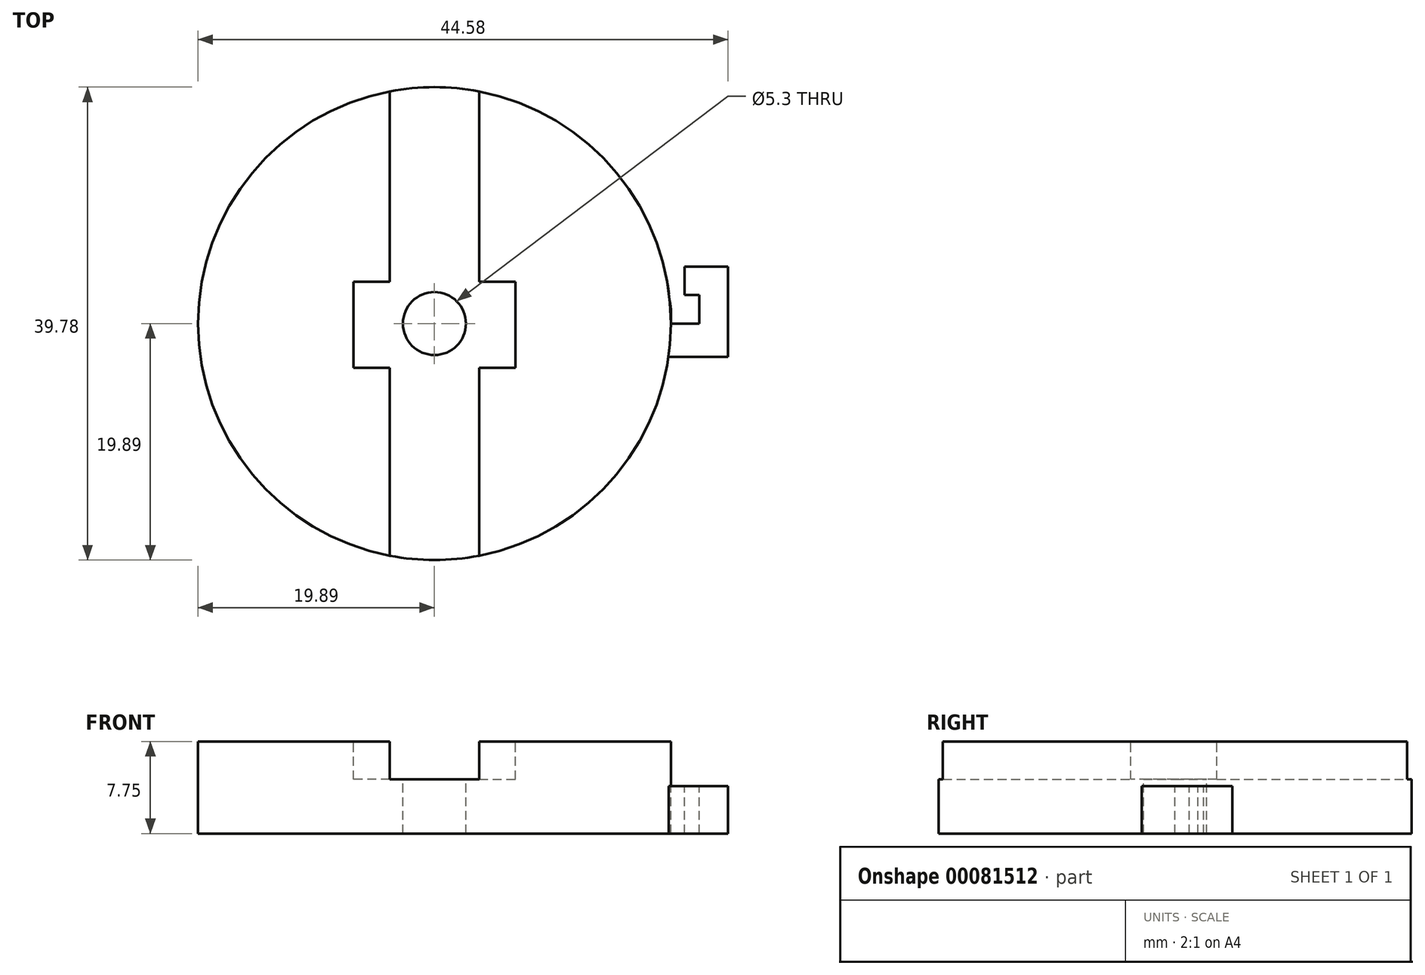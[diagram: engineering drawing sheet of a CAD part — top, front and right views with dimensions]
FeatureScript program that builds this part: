
annotation { "Feature Type Name" : "Feature", "Feature Type Description" : "" }
export const myFeature = defineFeature(function(context is Context, id is Id, definition is map)
    precondition{}
    {
        {
            var Q0;
            Q0=qCreatedBy(makeId("Top.planeOp"),FACE);
            var sketch = newSketch(context, id + "F0", { "sketchPlane" : qUnion([Q0])});
            skCircle(sketch, "E0", {"center": v(0, 0) * mm, "radius": 19.89 * mm});
            skSolve(sketch);
        }
        {
            var Q0;
            Q0 = qSketchRegion(id + "F0", true);
            extrude(context, id + "F1", {"entities" : qUnion([Q0]), "depth" : 7.75 * mm});
        }
        {
            var Q0;
            Q0=makeQuery(id+"F1.opExtrude","CAP_FACE",FACE,{"disambiguationData":[OSD([sQuery(id+"F0.wireOp",EDGE,"E0")])],"isStart":false});
            var sketch = newSketch(context, id + "F2", { "sketchPlane" : qUnion([Q0])});
            skLineSegment(sketch, "E1.bottom", {"start": v(3.75, -20.85) * mm, "end": v(-3.75, -20.85) * mm});
            skLineSegment(sketch, "E1.top", {"start": v(3.75, 20.85) * mm, "end": v(-3.75, 20.85) * mm});
            skLineSegment(sketch, "E1.left", {"start": v(3.75, -20.85) * mm, "end": v(3.75, 20.85) * mm});
            skLineSegment(sketch, "E1.right", {"start": v(-3.75, -20.85) * mm, "end": v(-3.75, 20.85) * mm});
            skPoint(sketch, "E1.middle", {"position": v(0, 0) * mm});
            skLineSegment(sketch, "E2.bottom", {"start": v(3.75, 3.51) * mm, "end": v(6.81, 3.51) * mm});
            skLineSegment(sketch, "E2.top", {"start": v(3.75, -3.74) * mm, "end": v(6.81, -3.74) * mm});
            skLineSegment(sketch, "E2.left", {"start": v(3.75, 3.51) * mm, "end": v(3.75, -3.74) * mm});
            skLineSegment(sketch, "E2.right", {"start": v(6.81, 3.51) * mm, "end": v(6.81, -3.74) * mm});
            skLineSegment(sketch, "E3.bottom", {"start": v(-3.75, 3.51) * mm, "end": v(-6.81, 3.51) * mm});
            skLineSegment(sketch, "E3.top", {"start": v(-3.75, -3.74) * mm, "end": v(-6.8, -3.74) * mm});
            skLineSegment(sketch, "E3.left", {"start": v(-3.75, 3.51) * mm, "end": v(-3.75, -3.74) * mm});
            skLineSegment(sketch, "E3.right", {"start": v(-6.81, 3.51) * mm, "end": v(-6.8, -3.74) * mm});
            skSolve(sketch);
        }
        {
            var Q0;
            Q0 = qSketchRegion(id + "F2", true);
            extrude(context, id + "F3", {"entities" : qUnion([Q0]), "operationType" : NewBodyOperationType.REMOVE, "oppositeDirection" : true, "depth" : 3.2 * mm});
        }
        {
            var Q0;
            Q0=qCreatedBy(makeId("Right.planeOp"),FACE);
            var sketch = newSketch(context, id + "F4", { "sketchPlane" : qUnion([Q0])});
            skLineSegment(sketch, "E4.bottom", {"start": v(-2.8, 4) * mm, "end": v(0, 4) * mm});
            skLineSegment(sketch, "E4.top", {"start": v(-2.8, 0) * mm, "end": v(0, 0) * mm});
            skLineSegment(sketch, "E4.left", {"start": v(-2.8, 4) * mm, "end": v(-2.8, 0) * mm});
            skLineSegment(sketch, "E4.right", {"start": v(0, 4) * mm, "end": v(0, 0) * mm});
            skLineSegment(sketch, "E5.bottom", {"start": v(-2.8, 4) * mm, "end": v(5.4, 4) * mm});
            skLineSegment(sketch, "E5.top", {"start": v(-2.8, 0) * mm, "end": v(5.4, 0) * mm});
            skLineSegment(sketch, "E5.right", {"start": v(5.4, 4) * mm, "end": v(5.4, 0) * mm});
            skSolve(sketch);
        }
        {
            var Q0;
            Q0 = qSketchRegion(id + "F4", true);
            extrude(context, id + "F5", {"entities" : qUnion([Q0]), "operationType" : NewBodyOperationType.ADD, "depth" : 25.21 * mm});
        }
        {
            var Q0;
            Q0=makeQuery(id+"F5.opExtrude","SWEPT_FACE",FACE,{"disambiguationData":[OSD([sQuery(id+"F4.wireOp",EDGE,"E5.bottom")])]});
            var sketch = newSketch(context, id + "F6", { "sketchPlane" : qUnion([Q0])});
            skLineSegment(sketch, "E6.bottom", {"start": v(19.89, 0) * mm, "end": v(22.29, 0) * mm});
            skLineSegment(sketch, "E6.top", {"start": v(19.89, 2.4) * mm, "end": v(22.29, 2.4) * mm});
            skLineSegment(sketch, "E6.left", {"start": v(19.89, 0) * mm, "end": v(19.89, 2.4) * mm});
            skLineSegment(sketch, "E6.right", {"start": v(22.29, 0) * mm, "end": v(22.29, 2.4) * mm});
            skSolve(sketch);
        }
        {
            var Q0;
            Q0 = qSketchRegion(id + "F6", true);
            extrude(context, id + "F7", {"entities" : qUnion([Q0]), "operationType" : NewBodyOperationType.REMOVE, "oppositeDirection" : true, "depth" : 4 * mm});
        }
        {
            var Q0;
            Q0=makeQuery(id+"F5.opExtrude","SWEPT_FACE",FACE,{"disambiguationData":[OSD([sQuery(id+"F4.wireOp",EDGE,"E5.bottom")])]});
            var sketch = newSketch(context, id + "F8", { "sketchPlane" : qUnion([Q0])});
            skLineSegment(sketch, "E7", {"start": v(19.89, 0) * mm, "end": v(19.89, 5.4) * mm});
            skLineSegment(sketch, "E8", {"start": v(19.89, 5.4) * mm, "end": v(19.14, 5.4) * mm});
            skFitSpline(sketch, "E9", {"points": [v(19.14, 5.4) * mm, v(19.3, 4.79) * mm, v(19.44, 4.17) * mm, v(19.6, 3.4) * mm, v(19.72, 2.52) * mm, v(19.8, 1.92) * mm, v(19.89, 1.2) * mm, v(19.89, 0.38) * mm, v(19.89, 0) * mm], "startDerivative": vector(1.2, -5.13) * mm, "endDerivative": vector(0.05, -3.6) * mm});
            skSolve(sketch);
        }
        {
            var Q0;
            {var subQ11=sQuery(id+"F8.wireOp",EDGE,"E8");Q0=makeQuery(id+"F8.imprint","IMPRINT",FACE,{"disambiguationData":[TD([[makeQuery(id+"F8.imprint","IMPRINT",EDGE,{"derivedFrom":subQ11}),1.0]])]});}
            extrude(context, id + "F9", {"entities" : qUnion([Q0]), "operationType" : NewBodyOperationType.REMOVE, "endBound" : BoundingType.THROUGH_ALL, "oppositeDirection" : true, "depth" : 25 * mm});
        }
        {
            var Q0;
            {var subQ3=sQuery(id+"F4.wireOp",EDGE,"E5.bottom");var subQ4=makeQuery(id+"F5.opExtrude","SWEPT_FACE",FACE,{"disambiguationData":[OSD([subQ3])]});var subQ6=sQuery(id+"F4.wireOp",EDGE,"E4.left");Q0=makeQuery(id+"F9.boolean.opBoolean","SPLIT",FACE,{"disambiguationData":[TD([makeQuery(id+"F5.opExtrude","SWEPT_FACE",FACE,{"disambiguationData":[OSD([subQ6])]})])],"derivedFrom":subQ4});}
            var sketch = newSketch(context, id + "F10", { "sketchPlane" : qUnion([Q0])});
            skLineSegment(sketch, "E10", {"start": v(19.74, 2.4) * mm, "end": v(21.04, 2.4) * mm});
            skLineSegment(sketch, "E11", {"start": v(21.04, 2.4) * mm, "end": v(21.04, 5.4) * mm});
            skLineSegment(sketch, "E12", {"start": v(21.04, 5.4) * mm, "end": v(19.89, 5.4) * mm});
            skLineSegment(sketch, "E13", {"start": v(19.89, 5.4) * mm, "end": v(19.74, 2.4) * mm});
            skSolve(sketch);
        }
        {
            var Q0;
            Q0 = qSketchRegion(id + "F10", true);
            extrude(context, id + "F11", {"entities" : qUnion([Q0]), "operationType" : NewBodyOperationType.REMOVE, "endBound" : BoundingType.THROUGH_ALL, "oppositeDirection" : true, "depth" : 25 * mm});
        }
        {
            var Q0;
            {var subQ3=sQuery(id+"F4.wireOp",EDGE,"E5.bottom");var subQ4=makeQuery(id+"F5.opExtrude","SWEPT_FACE",FACE,{"disambiguationData":[OSD([subQ3])]});var subQ6=sQuery(id+"F4.wireOp",EDGE,"E4.left");Q0=makeQuery(id+"F9.boolean.opBoolean","SPLIT",FACE,{"disambiguationData":[TD([makeQuery(id+"F5.opExtrude","SWEPT_FACE",FACE,{"disambiguationData":[OSD([subQ6])]})])],"derivedFrom":subQ4});}
            var sketch = newSketch(context, id + "F12", { "sketchPlane" : qUnion([Q0])});
            skLineSegment(sketch, "E14.bottom", {"start": v(25.21, 5.4) * mm, "end": v(24.69, 5.4) * mm});
            skLineSegment(sketch, "E14.top", {"start": v(25.21, -2.8) * mm, "end": v(24.69, -2.8) * mm});
            skLineSegment(sketch, "E14.left", {"start": v(25.21, 5.4) * mm, "end": v(25.21, -2.8) * mm});
            skLineSegment(sketch, "E14.right", {"start": v(24.69, 4.8) * mm, "end": v(24.69, -2.8) * mm});
            skLineSegment(sketch, "E15.bottom", {"start": v(21.04, 5.4) * mm, "end": v(25.21, 5.4) * mm});
            skLineSegment(sketch, "E15.top", {"start": v(21.04, 4.8) * mm, "end": v(24.69, 4.8) * mm});
            skLineSegment(sketch, "E15.left", {"start": v(21.04, 5.4) * mm, "end": v(21.04, 4.8) * mm});
            skLineSegment(sketch, "E15.right", {"start": v(25.21, 5.4) * mm, "end": v(25.21, 4.8) * mm});
            skSolve(sketch);
        }
        {
            var Q0;
            Q0 = qSketchRegion(id + "F12", true);
            extrude(context, id + "F13", {"entities" : qUnion([Q0]), "operationType" : NewBodyOperationType.REMOVE, "endBound" : BoundingType.THROUGH_ALL, "oppositeDirection" : true, "depth" : 25 * mm});
        }
        {
            var Q0;
            Q0=makeQuery(id+"F3.boolean.opBoolean","COPY",FACE,{"derivedFrom":makeQuery(id+"F3.opExtrude","CAP_FACE",FACE,{"disambiguationData":[OSD([sQuery(id+"F2.wireOp",EDGE,"E1.bottom"),sQuery(id+"F2.wireOp",EDGE,"E1.top"),sQuery(id+"F2.wireOp",EDGE,"E1.left"),sQuery(id+"F2.wireOp",EDGE,"E1.right"),sQuery(id+"F2.wireOp",EDGE,"E2.bottom"),sQuery(id+"F2.wireOp",EDGE,"E2.top"),sQuery(id+"F2.wireOp",EDGE,"E2.right"),sQuery(id+"F2.wireOp",EDGE,"E3.bottom"),sQuery(id+"F2.wireOp",EDGE,"E3.top"),sQuery(id+"F2.wireOp",EDGE,"E3.right")])],"isStart":false})});
            var sketch = newSketch(context, id + "F14", { "sketchPlane" : qUnion([Q0])});
            skCircle(sketch, "E16", {"center": v(0, 0) * mm, "radius": 2.65 * mm});
            skSolve(sketch);
        }
        {
            var Q0;
            Q0 = qSketchRegion(id + "F14", true);
            extrude(context, id + "F15", {"entities" : qUnion([Q0]), "operationType" : NewBodyOperationType.REMOVE, "endBound" : BoundingType.THROUGH_ALL, "oppositeDirection" : true, "depth" : 4.2 * mm});
        }
    });
